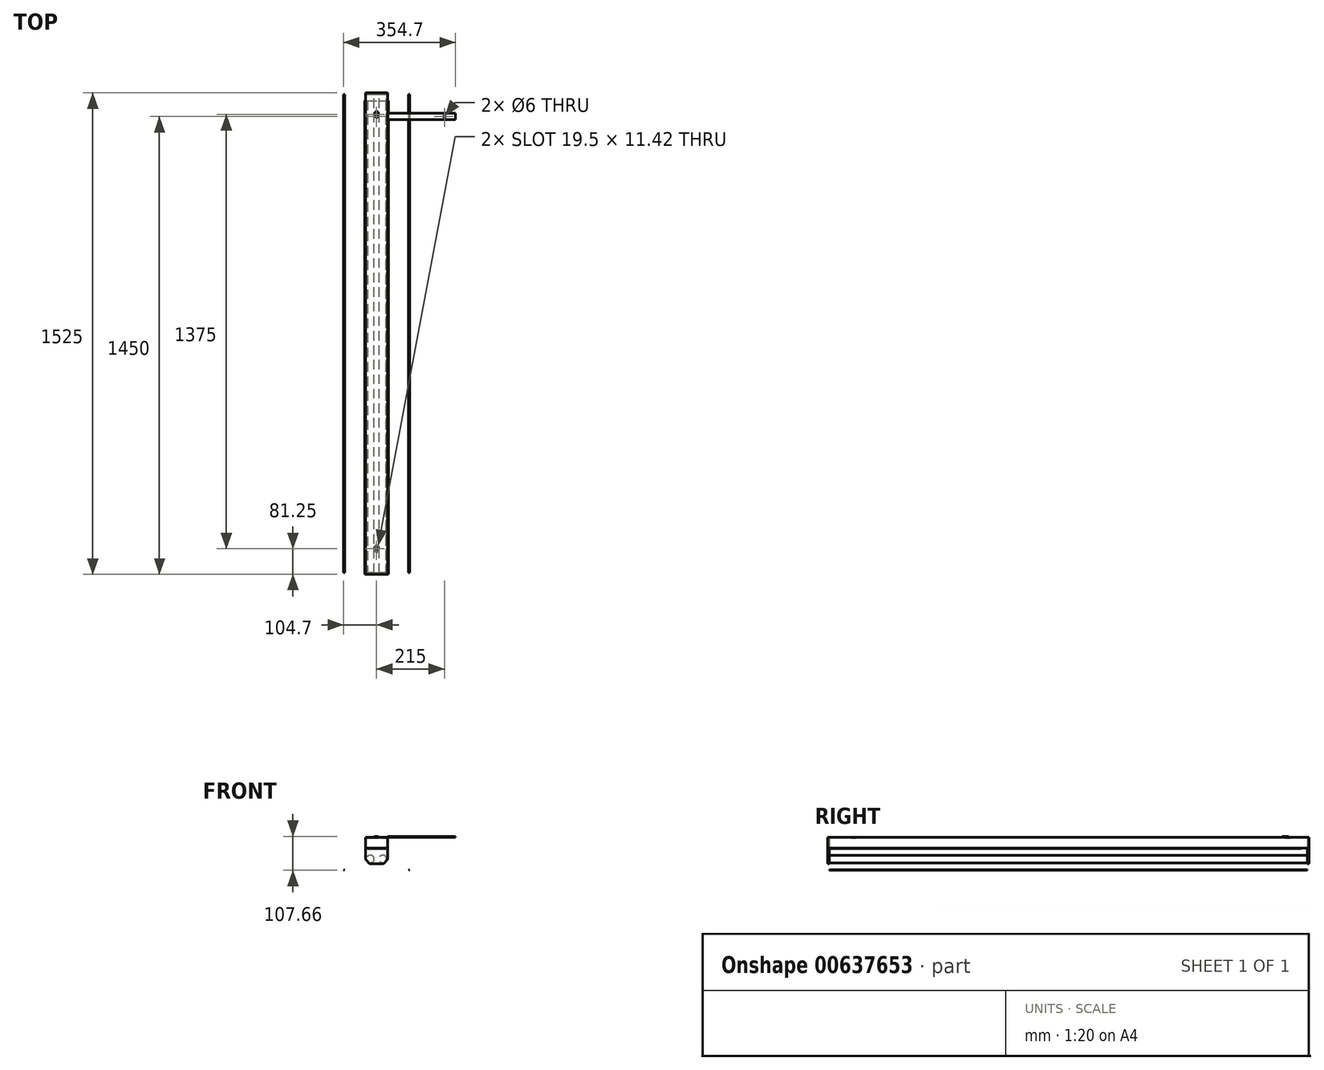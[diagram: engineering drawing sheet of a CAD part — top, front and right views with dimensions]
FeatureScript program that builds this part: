
annotation { "Feature Type Name" : "Feature", "Feature Type Description" : "" }
export const myFeature = defineFeature(function(context is Context, id is Id, definition is map)
    precondition{}
    {
        {
            var Q0;
            Q0=qCreatedBy(makeId("Front.planeOp"),FACE);
            var sketch = newSketch(context, id + "F0", { "sketchPlane" : qUnion([Q0])});
            skLineSegment(sketch, "E0", {"start": v(-35, 84) * mm, "end": v(35, 84) * mm});
            skLineSegment(sketch, "E1", {"start": v(35, 84) * mm, "end": v(35, 14) * mm});
            skLineSegment(sketch, "E2", {"start": v(22, 0) * mm, "end": v(35, 14) * mm});
            skLineSegment(sketch, "E3", {"start": v(22, 0) * mm, "end": v(-22, 0) * mm});
            skLineSegment(sketch, "E4", {"start": v(-22, 0) * mm, "end": v(-35, 14) * mm});
            skLineSegment(sketch, "E5", {"start": v(-35, 14) * mm, "end": v(-35, 84) * mm});
            skLineSegment(sketch, "E6", {"start": v(0, 44.81) * mm, "end": v(0, -20.6) * mm, "construction": true});
            skSolve(sketch);
        }
        {
            var Q0;
            Q0=makeQuery(id+"F0.imprint","IMPRINT",FACE,{"disambiguationData":[TD([[makeQuery(id+"F0.imprint","IMPRINT",EDGE,{"derivedFrom":sQuery(id+"F0.wireOp",EDGE,"E0")}),-1.0]])]});
            extrude(context, id + "F1", {"entities" : qUnion([Q0]), "oppositeDirection" : true, "depth" : 1525 * mm, "offsetDistance" : 25 * mm});
        }
        {
            var Q0;
            Q0=makeQuery(id+"F1.opExtrude","SWEPT_FACE",FACE,{"disambiguationData":[OSD([sQuery(id+"F0.wireOp",EDGE,"E1")])]});
            var sketch = newSketch(context, id + "F2", { "sketchPlane" : qUnion([Q0])});
            skLineSegment(sketch, "E7.bottom", {"start": v(5, 50) * mm, "end": v(1520, 50) * mm});
            skLineSegment(sketch, "E7.top", {"start": v(5, 0) * mm, "end": v(1520, 0) * mm});
            skLineSegment(sketch, "E7.left", {"start": v(5, 50) * mm, "end": v(5, 0) * mm});
            skLineSegment(sketch, "E7.right", {"start": v(1520, 50) * mm, "end": v(1520, 0) * mm});
            skSolve(sketch);
        }
        {
            var Q0;
            Q0=qSketchRegion(id+"F2",true);
            extrude(context, id + "F3", {"entities" : qUnion([Q0]), "operationType" : NewBodyOperationType.REMOVE, "oppositeDirection" : true, "depth" : 80 * mm, "offsetDistance" : 25 * mm});
        }
        {
            var Q0;
            Q0=makeQuery(id+"F3.boolean.opBoolean","COPY",FACE,{"derivedFrom":makeQuery(id+"F3.opExtrude","SWEPT_FACE",FACE,{"disambiguationData":[OSD([sQuery(id+"F2.wireOp",EDGE,"E7.right")])]})});
            var sketch = newSketch(context, id + "F4", { "sketchPlane" : qUnion([Q0])});
            skCircle(sketch, "E8", {"center": v(-19.7, 15.17) * mm, "radius": 12 * mm});
            skCircle(sketch, "E9", {"center": v(19.7, 15.17) * mm, "radius": 12 * mm});
            skLineSegment(sketch, "E10", {"start": v(-28.5, 7) * mm, "end": v(0, 33.46) * mm, "construction": true});
            skPoint(sketch, "E10.startSnap0", {"position": v(-28.5, 7) * mm});
            skLineSegment(sketch, "E11", {"start": v(0, 33.46) * mm, "end": v(28.5, 7) * mm, "construction": true});
            skSolve(sketch);
        }
        {
            var Q0;
            Q0=makeQuery(id+"F4.imprint","IMPRINT",FACE,{"disambiguationData":[TD([[makeQuery(id+"F4.imprint","IMPRINT",EDGE,{"derivedFrom":sQuery(id+"F4.wireOp",EDGE,"E8")}),1.0]])]});
            var Q1;
            Q1=makeQuery(id+"F4.imprint","IMPRINT",FACE,{"disambiguationData":[TD([[makeQuery(id+"F4.imprint","IMPRINT",EDGE,{"derivedFrom":sQuery(id+"F4.wireOp",EDGE,"E9")}),1.0]])]});
            var Q2;
            Q2=makeQuery(id+"F3.boolean.opBoolean","COPY",FACE,{"derivedFrom":makeQuery(id+"F3.opExtrude","SWEPT_FACE",FACE,{"disambiguationData":[OSD([sQuery(id+"F2.wireOp",EDGE,"E7.left")])]})});
            extrude(context, id + "F5", {"entities" : qUnion([Q0, Q1]), "operationType" : NewBodyOperationType.ADD, "endBound" : BoundingType.UP_TO_SURFACE, "depth" : 25 * mm, "endBoundEntityFace" : qUnion([Q2]), "offsetDistance" : 25 * mm});
        }
        {
            var Q0;
            Q0=makeQuery(id+"F1.opExtrude","SWEPT_FACE",FACE,{"disambiguationData":[OSD([sQuery(id+"F0.wireOp",EDGE,"E0")])]});
            var sketch = newSketch(context, id + "F6", { "sketchPlane" : qUnion([Q0])});
            skArc(sketch, "E12", {"start": v(-3.5, 75) * mm, "mid": v(0, 71.5) * mm, "end": v(3.5, 75) * mm});
            skArc(sketch, "E13", {"start": v(3.5, 80.13) * mm, "mid": v(0, 91) * mm, "end": v(-3.5, 80.13) * mm});
            skLineSegment(sketch, "E14", {"start": v(-3.5, 75) * mm, "end": v(-3.5, 80.13) * mm});
            skLineSegment(sketch, "E15", {"start": v(3.5, 75) * mm, "end": v(3.5, 80.13) * mm});
            skArc(sketch, "E16", {"start": v(-3.5, 1450) * mm, "mid": v(0, 1446.5) * mm, "end": v(3.5, 1450) * mm});
            skArc(sketch, "E17", {"start": v(3.5, 1455.13) * mm, "mid": v(0, 1466) * mm, "end": v(-3.5, 1455.13) * mm});
            skLineSegment(sketch, "E18", {"start": v(-3.5, 1450) * mm, "end": v(-3.5, 1455.13) * mm});
            skLineSegment(sketch, "E19", {"start": v(3.5, 1450) * mm, "end": v(3.5, 1455.13) * mm});
            skSolve(sketch);
        }
        {
            var Q0;
            Q0=makeQuery(id+"F3.boolean.opBoolean","COPY",FACE,{"derivedFrom":makeQuery(id+"F3.opExtrude","SWEPT_FACE",FACE,{"disambiguationData":[OSD([sQuery(id+"F2.wireOp",EDGE,"E7.bottom")])]})});
            var sketch = newSketch(context, id + "F7", { "sketchPlane" : qUnion([Q0])});
            skLineSegment(sketch, "E20.bottom", {"start": v(-33, -1520) * mm, "end": v(33, -1520) * mm});
            skLineSegment(sketch, "E20.top", {"start": v(-33, -5) * mm, "end": v(33, -5) * mm});
            skLineSegment(sketch, "E20.left", {"start": v(-33, -1520) * mm, "end": v(-33, -5) * mm});
            skLineSegment(sketch, "E20.right", {"start": v(33, -1520) * mm, "end": v(33, -5) * mm});
            skSolve(sketch);
        }
        {
            var Q0;
            Q0=qSketchRegion(id+"F7",true);
            extrude(context, id + "F8", {"entities" : qUnion([Q0]), "operationType" : NewBodyOperationType.REMOVE, "oppositeDirection" : true, "depth" : 32 * mm, "offsetDistance" : 25 * mm});
        }
        {
            var Q0;
            Q0=qSketchRegion(id+"F6",true);
            var Q1;
            Q1=makeQuery(id+"F8.boolean.opBoolean","COPY",FACE,{"derivedFrom":makeQuery(id+"F8.opExtrude","CAP_FACE",FACE,{"disambiguationData":[OSD([sQuery(id+"F7.wireOp",EDGE,"E20.bottom"),sQuery(id+"F7.wireOp",EDGE,"E20.top"),sQuery(id+"F7.wireOp",EDGE,"E20.left"),sQuery(id+"F7.wireOp",EDGE,"E20.right")])],"isStart":false})});
            extrude(context, id + "F9", {"entities" : qUnion([Q0]), "operationType" : NewBodyOperationType.REMOVE, "endBound" : BoundingType.UP_TO_SURFACE, "oppositeDirection" : true, "depth" : 25 * mm, "endBoundEntityFace" : qUnion([Q1]), "offsetDistance" : 25 * mm});
        }
        {
            var Q0;
            Q0=qCreatedBy(makeId("Front.planeOp"),FACE);
            var sketch = newSketch(context, id + "F10", { "sketchPlane" : qUnion([Q0])});
            skLineSegment(sketch, "E21", {"start": v(-40, -21) * mm, "end": v(-40, 49) * mm, "construction": true});
            skFitSpline(sketch, "E22", {"points": [v(-100, -21) * mm, v(-40, 49) * mm, v(20, -21) * mm], "startDerivative": vector(120, 360) * mm, "endDerivative": vector(120, -360) * mm});
            skLineSegment(sketch, "E23", {"start": v(-100, -21) * mm, "end": v(-104.7, -19.29) * mm});
            skLineSegment(sketch, "E24", {"start": v(20, -21) * mm, "end": v(24.7, -19.29) * mm});
            skLineSegment(sketch, "E25", {"start": v(-100, -21) * mm, "end": v(20, -21) * mm, "construction": true});
            skFitSpline(sketch, "E26.0", {"points": [v(-100.95, -20.68) * mm, v(-95.94, -5.64) * mm, v(-88.4, 12.24) * mm, v(-78.32, 28.64) * mm, v(-70.72, 37.68) * mm, v(-63.06, 43.9) * mm, v(-55.35, 47.76) * mm, v(-48.93, 49.36) * mm, v(-43.82, 49.92) * mm, v(-40, 50.04) * mm, v(-36.18, 49.92) * mm, v(-31.07, 49.36) * mm, v(-24.65, 47.76) * mm, v(-16.94, 43.9) * mm, v(-9.28, 37.68) * mm, v(-1.68, 28.64) * mm, v(8.4, 12.24) * mm, v(15.94, -5.64) * mm, v(20.95, -20.68) * mm]});
            skLineSegment(sketch, "E27.0", {"start": v(-99.66, -20.06) * mm, "end": v(-99.68, -20.05) * mm});
            skLineSegment(sketch, "E28.0", {"start": v(19.66, -20.06) * mm, "end": v(19.68, -20.05) * mm});
            skLineSegment(sketch, "E29", {"start": v(24.36, -18.35) * mm, "end": v(24.7, -19.29) * mm});
            skLineSegment(sketch, "E30", {"start": v(-104.36, -18.35) * mm, "end": v(-104.7, -19.29) * mm});
            skFitSpline(sketch, "E31.trimOffspring", {"points": [v(-100.95, -20.68) * mm, v(-95.94, -5.64) * mm, v(-88.4, 12.24) * mm, v(-78.32, 28.64) * mm, v(-70.72, 37.68) * mm, v(-63.06, 43.9) * mm, v(-55.35, 47.76) * mm, v(-48.93, 49.36) * mm, v(-43.82, 49.92) * mm, v(-40, 50.04) * mm, v(-36.18, 49.92) * mm, v(-31.07, 49.36) * mm, v(-24.65, 47.76) * mm, v(-16.94, 43.9) * mm, v(-9.28, 37.68) * mm, v(-1.68, 28.64) * mm, v(8.4, 12.24) * mm, v(15.94, -5.64) * mm, v(20.95, -20.68) * mm]});
            skLineSegment(sketch, "E32.trimOffspring", {"start": v(-100.62, -19.7) * mm, "end": v(-104.36, -18.35) * mm});
            skFitSpline(sketch, "E33.trimOffspring", {"points": [v(-100.95, -20.68) * mm, v(-95.94, -5.64) * mm, v(-88.4, 12.24) * mm, v(-78.32, 28.64) * mm, v(-70.72, 37.68) * mm, v(-63.06, 43.9) * mm, v(-55.35, 47.76) * mm, v(-48.93, 49.36) * mm, v(-43.82, 49.92) * mm, v(-40, 50.04) * mm, v(-36.18, 49.92) * mm, v(-31.07, 49.36) * mm, v(-24.65, 47.76) * mm, v(-16.94, 43.9) * mm, v(-9.28, 37.68) * mm, v(-1.68, 28.64) * mm, v(8.4, 12.24) * mm, v(15.94, -5.64) * mm, v(20.95, -20.68) * mm]});
            skLineSegment(sketch, "E34.trimOffspring", {"start": v(20.62, -19.7) * mm, "end": v(24.36, -18.35) * mm});
            skLineSegment(sketch, "E35", {"start": v(40, -21) * mm, "end": v(40, 49) * mm, "construction": true});
            skFitSpline(sketch, "E36", {"points": [v(-20, -21) * mm, v(40, 49) * mm, v(100, -21) * mm], "startDerivative": vector(120, 360) * mm, "endDerivative": vector(120, -360) * mm});
            skLineSegment(sketch, "E37", {"start": v(-20, -21) * mm, "end": v(-24.7, -19.29) * mm});
            skLineSegment(sketch, "E38", {"start": v(100, -21) * mm, "end": v(104.7, -19.29) * mm});
            skLineSegment(sketch, "E39", {"start": v(-20, -21) * mm, "end": v(100, -21) * mm, "construction": true});
            skFitSpline(sketch, "E40.0", {"points": [v(-20.95, -20.68) * mm, v(-15.94, -5.64) * mm, v(-8.4, 12.24) * mm, v(1.68, 28.64) * mm, v(9.28, 37.68) * mm, v(16.94, 43.9) * mm, v(24.65, 47.76) * mm, v(31.07, 49.36) * mm, v(36.18, 49.92) * mm, v(40, 50.04) * mm, v(43.82, 49.92) * mm, v(48.93, 49.36) * mm, v(55.35, 47.76) * mm, v(63.06, 43.9) * mm, v(70.72, 37.68) * mm, v(78.32, 28.64) * mm, v(88.4, 12.24) * mm, v(95.94, -5.64) * mm, v(100.95, -20.68) * mm]});
            skLineSegment(sketch, "E41.0", {"start": v(-19.66, -20.06) * mm, "end": v(-19.68, -20.05) * mm});
            skLineSegment(sketch, "E42.0", {"start": v(99.66, -20.06) * mm, "end": v(99.68, -20.05) * mm});
            skLineSegment(sketch, "E43", {"start": v(104.36, -18.35) * mm, "end": v(104.7, -19.29) * mm});
            skLineSegment(sketch, "E44", {"start": v(-24.36, -18.35) * mm, "end": v(-24.7, -19.29) * mm});
            skFitSpline(sketch, "E45.trimOffspring", {"points": [v(-20.95, -20.68) * mm, v(-15.94, -5.64) * mm, v(-8.4, 12.24) * mm, v(1.68, 28.64) * mm, v(9.28, 37.68) * mm, v(16.94, 43.9) * mm, v(24.65, 47.76) * mm, v(31.07, 49.36) * mm, v(36.18, 49.92) * mm, v(40, 50.04) * mm, v(43.82, 49.92) * mm, v(48.93, 49.36) * mm, v(55.35, 47.76) * mm, v(63.06, 43.9) * mm, v(70.72, 37.68) * mm, v(78.32, 28.64) * mm, v(88.4, 12.24) * mm, v(95.94, -5.64) * mm, v(100.95, -20.68) * mm]});
            skLineSegment(sketch, "E46.trimOffspring", {"start": v(-20.62, -19.7) * mm, "end": v(-24.36, -18.35) * mm});
            skFitSpline(sketch, "E47.trimOffspring", {"points": [v(-20.95, -20.68) * mm, v(-15.94, -5.64) * mm, v(-8.4, 12.24) * mm, v(1.68, 28.64) * mm, v(9.28, 37.68) * mm, v(16.94, 43.9) * mm, v(24.65, 47.76) * mm, v(31.07, 49.36) * mm, v(36.18, 49.92) * mm, v(40, 50.04) * mm, v(43.82, 49.92) * mm, v(48.93, 49.36) * mm, v(55.35, 47.76) * mm, v(63.06, 43.9) * mm, v(70.72, 37.68) * mm, v(78.32, 28.64) * mm, v(88.4, 12.24) * mm, v(95.94, -5.64) * mm, v(100.95, -20.68) * mm]});
            skLineSegment(sketch, "E48.trimOffspring", {"start": v(100.62, -19.7) * mm, "end": v(104.36, -18.35) * mm});
            skLineSegment(sketch, "E49", {"start": v(-40, 50) * mm, "end": v(40, 50) * mm});
            skLineSegment(sketch, "E50", {"start": v(-40, 49) * mm, "end": v(40, 49) * mm});
            skSolve(sketch);
        }
        {
            var Q0;
            {var subQ0=sQuery(id+"F10.wireOp",EDGE,"E49");Q0=makeQuery(id+"F10.imprint","IMPRINT",FACE,{"disambiguationData":[TD([[makeQuery(id+"F10.imprint","IMPRINT",EDGE,{"derivedFrom":subQ0}),-1.0]])]});}
            var Q1;
            {var subQ0=sQuery(id+"F10.wireOp",EDGE,"E30");Q1=makeQuery(id+"F10.imprint","IMPRINT",FACE,{"disambiguationData":[TD([[makeQuery(id+"F10.imprint","IMPRINT",EDGE,{"derivedFrom":subQ0}),1.0]])]});}
            var Q2;
            {var subQ5=sQuery(id+"F10.wireOp",EDGE,"E43");Q2=makeQuery(id+"F10.imprint","IMPRINT",FACE,{"disambiguationData":[TD([[makeQuery(id+"F10.imprint","IMPRINT",EDGE,{"derivedFrom":subQ5}),-1.0]])]});}
            extrude(context, id + "F11", {"entities" : qUnion([Q0, Q1, Q2]), "oppositeDirection" : true, "depth" : 1500 * mm, "offsetDistance" : 25 * mm});
        }
        {
            var Q0;
            Q0=makeQuery(id+"F11.opExtrude","CAP_FACE",FACE,{"disambiguationData":[OSD([sQuery(id+"F10.wireOp",EDGE,"E22"),sQuery(id+"F10.wireOp",EDGE,"E23"),sQuery(id+"F10.wireOp",EDGE,"E30"),sQuery(id+"F10.wireOp",EDGE,"E31.trimOffspring"),sQuery(id+"F10.wireOp",EDGE,"E32.trimOffspring"),sQuery(id+"F10.wireOp",EDGE,"E36"),sQuery(id+"F10.wireOp",EDGE,"E38"),sQuery(id+"F10.wireOp",EDGE,"E43"),sQuery(id+"F10.wireOp",EDGE,"E45.trimOffspring"),sQuery(id+"F10.wireOp",EDGE,"E48.trimOffspring"),sQuery(id+"F10.wireOp",EDGE,"E49"),sQuery(id+"F10.wireOp",EDGE,"E50")])],"isStart":false});
            var Q1;
            Q1=makeQuery(id+"F8.boolean.opBoolean","MERGE",FACE,{"derivedFrom":[makeQuery(id+"F3.boolean.opBoolean","COPY",FACE,{"derivedFrom":makeQuery(id+"F3.opExtrude","SWEPT_FACE",FACE,{"disambiguationData":[OSD([sQuery(id+"F2.wireOp",EDGE,"E7.right")])]})}),makeQuery(id+"F8.opExtrude","SWEPT_FACE",FACE,{"disambiguationData":[OSD([sQuery(id+"F7.wireOp",EDGE,"E20.bottom")])]})]});
            extrude(context, id + "F12", {"entities" : qUnion([Q0]), "operationType" : NewBodyOperationType.ADD, "endBound" : BoundingType.UP_TO_SURFACE, "depth" : 25 * mm, "endBoundEntityFace" : qUnion([Q1]), "offsetDistance" : 25 * mm});
        }
        {
            var Q0;
            Q0=makeQuery(id+"F11.opExtrude","CAP_FACE",FACE,{"disambiguationData":[OSD([sQuery(id+"F10.wireOp",EDGE,"E22"),sQuery(id+"F10.wireOp",EDGE,"E23"),sQuery(id+"F10.wireOp",EDGE,"E30"),sQuery(id+"F10.wireOp",EDGE,"E31.trimOffspring"),sQuery(id+"F10.wireOp",EDGE,"E32.trimOffspring"),sQuery(id+"F10.wireOp",EDGE,"E36"),sQuery(id+"F10.wireOp",EDGE,"E38"),sQuery(id+"F10.wireOp",EDGE,"E43"),sQuery(id+"F10.wireOp",EDGE,"E45.trimOffspring"),sQuery(id+"F10.wireOp",EDGE,"E48.trimOffspring"),sQuery(id+"F10.wireOp",EDGE,"E49"),sQuery(id+"F10.wireOp",EDGE,"E50")])],"isStart":true});
            var Q1;
            Q1=makeQuery(id+"F8.boolean.opBoolean","MERGE",FACE,{"derivedFrom":[makeQuery(id+"F3.boolean.opBoolean","COPY",FACE,{"derivedFrom":makeQuery(id+"F3.opExtrude","SWEPT_FACE",FACE,{"disambiguationData":[OSD([sQuery(id+"F2.wireOp",EDGE,"E7.left")])]})}),makeQuery(id+"F8.opExtrude","SWEPT_FACE",FACE,{"disambiguationData":[OSD([sQuery(id+"F7.wireOp",EDGE,"E20.top")])]})]});
            extrude(context, id + "F13", {"entities" : qUnion([Q0]), "operationType" : NewBodyOperationType.REMOVE, "endBound" : BoundingType.UP_TO_SURFACE, "oppositeDirection" : true, "depth" : 25 * mm, "endBoundEntityFace" : qUnion([Q1]), "offsetDistance" : 25 * mm});
        }
        {
            var Q0;
            Q0=makeQuery(id+"F1.opExtrude","SWEPT_FACE",FACE,{"disambiguationData":[OSD([sQuery(id+"F0.wireOp",EDGE,"E0")])]});
            var sketch = newSketch(context, id + "F14", { "sketchPlane" : qUnion([Q0])});
            skLineSegment(sketch, "E51.0", {"start": v(104.7, 1520) * mm, "end": v(104.7, 5) * mm});
            skLineSegment(sketch, "E52.0", {"start": v(-35, 1525) * mm, "end": v(-35, 0) * mm});
            skLineSegment(sketch, "E53.bottom", {"start": v(250, 1440) * mm, "end": v(-35, 1440) * mm});
            skLineSegment(sketch, "E53.top", {"start": v(250, 1460) * mm, "end": v(-35, 1460) * mm});
            skLineSegment(sketch, "E53.left", {"start": v(250, 1440) * mm, "end": v(250, 1460) * mm});
            skLineSegment(sketch, "E53.right", {"start": v(-35, 1440) * mm, "end": v(-35, 1460) * mm});
            skArc(sketch, "E54.0", {"start": v(-3.5, 1450) * mm, "mid": v(0, 1446.5) * mm, "end": v(3.5, 1450) * mm});
            skCircle(sketch, "E55", {"center": v(0, 1450) * mm, "radius": 3 * mm});
            skCircle(sketch, "E56", {"center": v(215, 1450) * mm, "radius": 3 * mm});
            skSolve(sketch);
        }
        {
            var Q0;
            {var subQ0=sQuery(id+"F14.wireOp",EDGE,"E53.left");Q0=makeQuery(id+"F14.imprint","IMPRINT",FACE,{"disambiguationData":[TD([[makeQuery(id+"F14.imprint","IMPRINT",EDGE,{"derivedFrom":subQ0}),1.0]])]});}
            var Q1;
            {var subQ0=sQuery(id+"F14.wireOp",EDGE,"E53.bottom");var subQ1=sQuery(id+"F14.wireOp",EDGE,"E51.0");var subQ2=makeQuery(id+"F14.imprint","INTERSECT",VERTEX,{"derivedFrom":[subQ1,subQ0]});Q1=makeQuery(id+"F14.imprint","IMPRINT",FACE,{"disambiguationData":[TD([[makeQuery(id+"F14.imprint","IMPRINT",EDGE,{"disambiguationData":[TD([[subQ2,1.0]])],"derivedFrom":subQ1}),-1.0]])]});}
            var Q2;
            {var subQ0=sQuery(id+"F14.wireOp",EDGE,"E53.right");Q2=makeQuery(id+"F14.imprint","IMPRINT",FACE,{"disambiguationData":[TD([[makeQuery(id+"F14.imprint","IMPRINT",EDGE,{"derivedFrom":subQ0}),1.0]])]});}
            var Q3;
            Q3=makeQuery(id+"F14.imprint","IMPRINT",FACE,{"disambiguationData":[TD([[makeQuery(id+"F14.imprint","IMPRINT",EDGE,{"derivedFrom":sQuery(id+"F14.wireOp",EDGE,"E54.0")}),1.0]])]});
            extrude(context, id + "F15", {"entities" : qUnion([Q0, Q1, Q2, Q3]), "depth" : 3 * mm, "offsetDistance" : 25 * mm});
        }
    });
